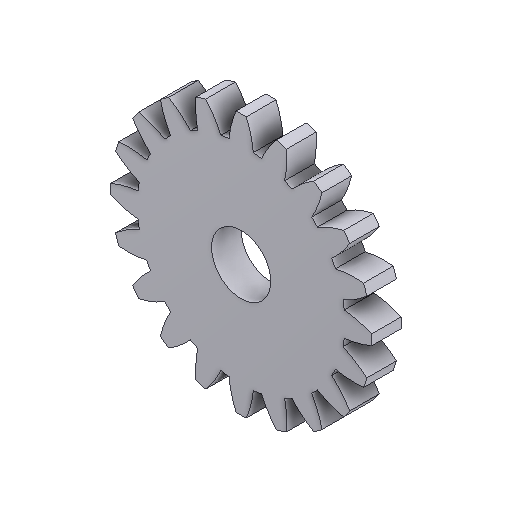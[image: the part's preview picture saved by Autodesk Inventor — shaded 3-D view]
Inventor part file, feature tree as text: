
AUTODESK INVENTOR PART (.ipt)
format: ipt  version: 2025.1 (Build 291241000, 241)  size: 313,856 bytes
history: native  units: mm
features: extrude x3, sketch x3, other x2
ambient origin geometry x8: Origin, YZ Plane, XZ Plane, XY Plane, X Axis, Y Axis, Z Axis, Center Point
bodies: Body1 (feature_tree)
feature tree (8):
  other  "Bryła1"
  extrude  "Wyciągnięcie proste1"  TaperAngle=0.0deg  [1 undecoded]
  extrude  "Wyciągnięcie proste2"  Depth=10.0mm TaperAngle=0.0deg
  extrude  "Wyciągnięcie proste3"  Depth=5.0mm TaperAngle=0.0deg
  sketch  "Szkic1"
  sketch  "Szkic2"
  sketch  "Szkic3"
  other  "Gea20.stp_1_"
note: 1 required parameter value undecoded (feature->parameter linkage not recoverable at this tier; creation-order binding heuristic only, values carry confidence <= 0.55)
